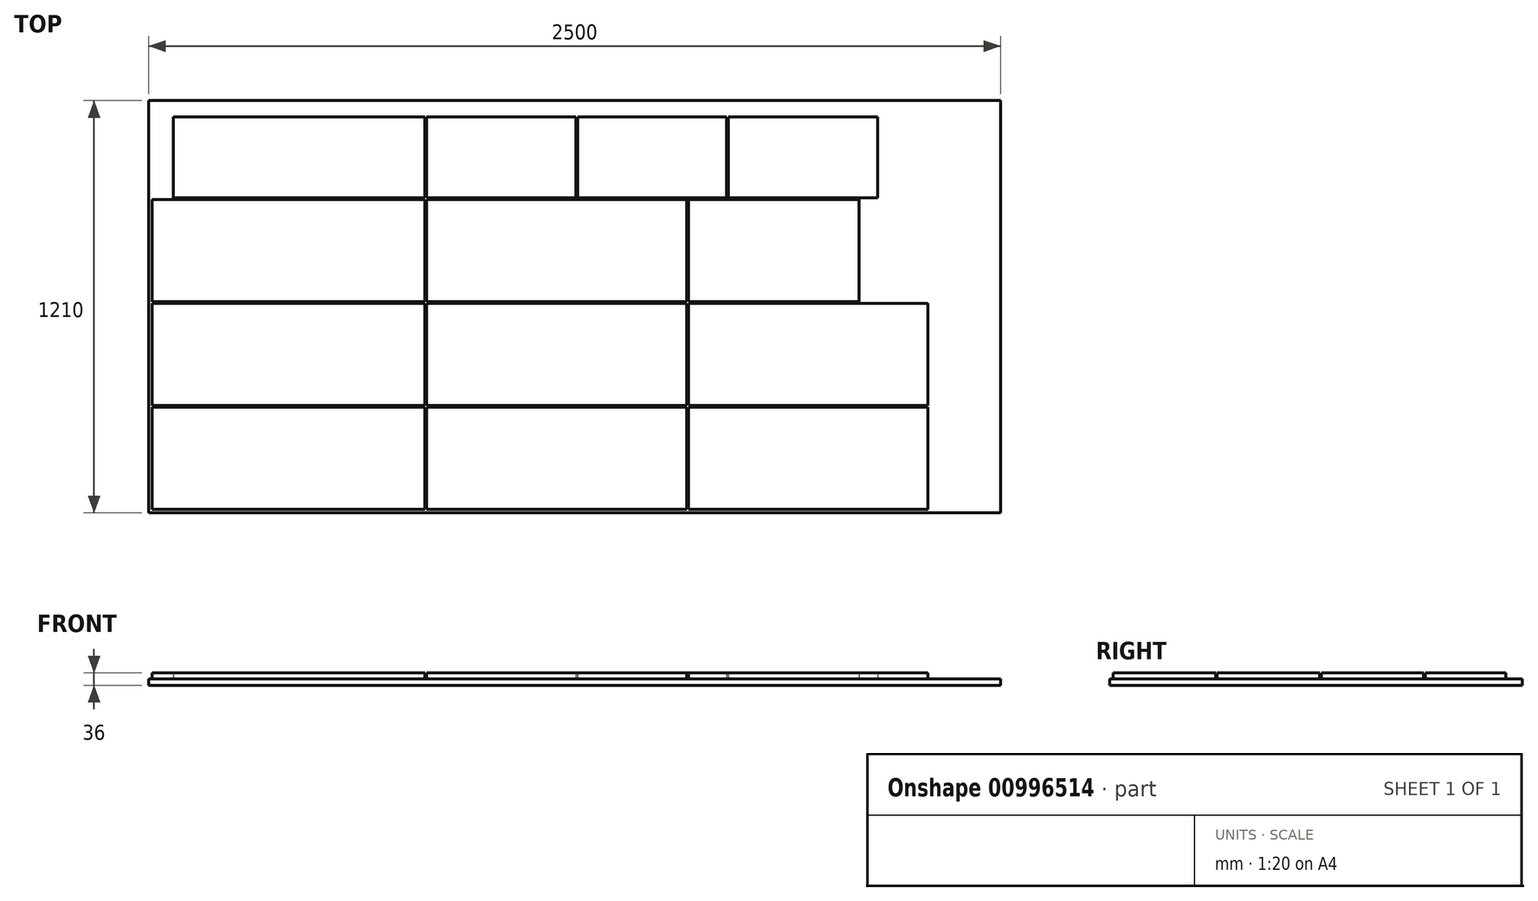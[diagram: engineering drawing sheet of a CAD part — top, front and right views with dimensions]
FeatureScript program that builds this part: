
annotation { "Feature Type Name" : "Feature", "Feature Type Description" : "" }
export const myFeature = defineFeature(function(context is Context, id is Id, definition is map)
    precondition{}
    {
        {
            var Q0;
            Q0=qCreatedBy(makeId("Top.planeOp"),FACE);
            var sketch = newSketch(context, id + "F0", { "sketchPlane" : qUnion([Q0])});
            skLineSegment(sketch, "E0.bottom", {"start": v(0, 0) * mm, "end": v(2500, 0) * mm});
            skLineSegment(sketch, "E0.top", {"start": v(0, 1210) * mm, "end": v(2500, 1210) * mm});
            skLineSegment(sketch, "E0.left", {"start": v(0, 0) * mm, "end": v(0, 1210) * mm});
            skLineSegment(sketch, "E0.right", {"start": v(2500, 0) * mm, "end": v(2500, 1210) * mm});
            skSolve(sketch);
        }
        {
            var Q0;
            Q0=makeQuery(id+"F0.imprint","IMPRINT",FACE,{"disambiguationData":[TD([[makeQuery(id+"F0.imprint","IMPRINT",EDGE,{"derivedFrom":sQuery(id+"F0.wireOp",EDGE,"E0.bottom")}),1.0]])]});
            extrude(context, id + "F1", {"entities" : qUnion([Q0]), "depth" : 18 * mm, "offsetDistance" : 25 * mm});
        }
        {
            var Q0;
            Q0=makeQuery(id+"F1.opExtrude","CAP_FACE",FACE,{"disambiguationData":[OSD([sQuery(id+"F0.wireOp",EDGE,"E0.bottom"),sQuery(id+"F0.wireOp",EDGE,"E0.top"),sQuery(id+"F0.wireOp",EDGE,"E0.left"),sQuery(id+"F0.wireOp",EDGE,"E0.right")])],"isStart":false});
            var sketch = newSketch(context, id + "F2", { "sketchPlane" : qUnion([Q0])});
            skLineSegment(sketch, "E1.bottom", {"start": v(10, 10) * mm, "end": v(810, 10) * mm});
            skLineSegment(sketch, "E1.top", {"start": v(10, 310) * mm, "end": v(810, 310) * mm});
            skLineSegment(sketch, "E1.left", {"start": v(10, 10) * mm, "end": v(10, 310) * mm});
            skLineSegment(sketch, "E1.right", {"start": v(810, 10) * mm, "end": v(810, 310) * mm});
            skLineSegment(sketch, "E2.bottom", {"start": v(10, 315) * mm, "end": v(810, 315) * mm});
            skLineSegment(sketch, "E2.top", {"start": v(10, 615) * mm, "end": v(810, 615) * mm});
            skLineSegment(sketch, "E2.left", {"start": v(10, 315) * mm, "end": v(10, 615) * mm});
            skLineSegment(sketch, "E2.right", {"start": v(810, 315) * mm, "end": v(810, 615) * mm});
            skLineSegment(sketch, "E3.bottom", {"start": v(10, 620) * mm, "end": v(810, 620) * mm});
            skLineSegment(sketch, "E3.top", {"start": v(10, 920) * mm, "end": v(810, 920) * mm});
            skLineSegment(sketch, "E3.left", {"start": v(10, 620) * mm, "end": v(10, 920) * mm});
            skLineSegment(sketch, "E3.right", {"start": v(810, 620) * mm, "end": v(810, 920) * mm});
            skLineSegment(sketch, "E4.bottom", {"start": v(815, 10) * mm, "end": v(1579, 10) * mm});
            skLineSegment(sketch, "E4.top", {"start": v(815, 310) * mm, "end": v(1579, 310) * mm});
            skLineSegment(sketch, "E4.left", {"start": v(815, 10) * mm, "end": v(815, 310) * mm});
            skLineSegment(sketch, "E4.right", {"start": v(1579, 10) * mm, "end": v(1579, 310) * mm});
            skLineSegment(sketch, "E5.bottom", {"start": v(815, 615) * mm, "end": v(1579, 615) * mm});
            skLineSegment(sketch, "E5.top", {"start": v(815, 315) * mm, "end": v(1579, 315) * mm});
            skLineSegment(sketch, "E5.left", {"start": v(815, 615) * mm, "end": v(815, 315) * mm});
            skLineSegment(sketch, "E5.right", {"start": v(1579, 615) * mm, "end": v(1579, 315) * mm});
            skLineSegment(sketch, "E6.bottom", {"start": v(815, 620) * mm, "end": v(1579, 620) * mm});
            skLineSegment(sketch, "E6.top", {"start": v(815, 920) * mm, "end": v(1579, 920) * mm});
            skLineSegment(sketch, "E6.left", {"start": v(815, 620) * mm, "end": v(815, 920) * mm});
            skLineSegment(sketch, "E6.right", {"start": v(1579, 620) * mm, "end": v(1579, 920) * mm});
            skLineSegment(sketch, "E7.bottom", {"start": v(72, 925) * mm, "end": v(810, 925) * mm});
            skLineSegment(sketch, "E7.top", {"start": v(72, 1162) * mm, "end": v(810, 1162) * mm});
            skLineSegment(sketch, "E7.left", {"start": v(72, 925) * mm, "end": v(72, 1162) * mm});
            skLineSegment(sketch, "E7.right", {"start": v(810, 925) * mm, "end": v(810, 1162) * mm});
            skLineSegment(sketch, "E8.bottom", {"start": v(815, 925) * mm, "end": v(1253, 925) * mm});
            skLineSegment(sketch, "E8.top", {"start": v(815, 1162) * mm, "end": v(1253, 1162) * mm});
            skLineSegment(sketch, "E8.left", {"start": v(815, 925) * mm, "end": v(815, 1162) * mm});
            skLineSegment(sketch, "E8.right", {"start": v(1253, 925) * mm, "end": v(1253, 1162) * mm});
            skLineSegment(sketch, "E9.bottom", {"start": v(1584, 310) * mm, "end": v(2286, 310) * mm});
            skLineSegment(sketch, "E9.top", {"start": v(1584, 10) * mm, "end": v(2286, 10) * mm});
            skLineSegment(sketch, "E9.left", {"start": v(1584, 310) * mm, "end": v(1584, 10) * mm});
            skLineSegment(sketch, "E9.right", {"start": v(2286, 310) * mm, "end": v(2286, 10) * mm});
            skLineSegment(sketch, "E10.bottom", {"start": v(1584, 615) * mm, "end": v(2286, 615) * mm});
            skLineSegment(sketch, "E10.top", {"start": v(1584, 315) * mm, "end": v(2286, 315) * mm});
            skLineSegment(sketch, "E10.left", {"start": v(1584, 615) * mm, "end": v(1584, 315) * mm});
            skLineSegment(sketch, "E10.right", {"start": v(2286, 615) * mm, "end": v(2286, 315) * mm});
            skLineSegment(sketch, "E11.bottom", {"start": v(1584, 920) * mm, "end": v(2084, 920) * mm});
            skLineSegment(sketch, "E11.top", {"start": v(1584, 620) * mm, "end": v(2084, 620) * mm});
            skLineSegment(sketch, "E11.left", {"start": v(1584, 920) * mm, "end": v(1584, 620) * mm});
            skLineSegment(sketch, "E11.right", {"start": v(2084, 920) * mm, "end": v(2084, 620) * mm});
            skLineSegment(sketch, "E12.bottom", {"start": v(1258, 1162) * mm, "end": v(1696, 1162) * mm});
            skLineSegment(sketch, "E12.top", {"start": v(1258, 925) * mm, "end": v(1696, 925) * mm});
            skLineSegment(sketch, "E12.left", {"start": v(1258, 1162) * mm, "end": v(1258, 925) * mm});
            skLineSegment(sketch, "E12.right", {"start": v(1696, 1162) * mm, "end": v(1696, 925) * mm});
            skLineSegment(sketch, "E13.bottom", {"start": v(1701, 1162) * mm, "end": v(2139, 1162) * mm});
            skLineSegment(sketch, "E13.top", {"start": v(1701, 925) * mm, "end": v(2139, 925) * mm});
            skLineSegment(sketch, "E13.left", {"start": v(1701, 1162) * mm, "end": v(1701, 925) * mm});
            skLineSegment(sketch, "E13.right", {"start": v(2139, 1162) * mm, "end": v(2139, 925) * mm});
            skSolve(sketch);
        }
        {
            var Q0;
            Q0=makeQuery(id+"F2.imprint","IMPRINT",FACE,{"disambiguationData":[TD([[makeQuery(id+"F2.imprint","IMPRINT",EDGE,{"derivedFrom":sQuery(id+"F2.wireOp",EDGE,"E7.bottom")}),1.0]])]});
            var Q1;
            Q1=makeQuery(id+"F2.imprint","IMPRINT",FACE,{"disambiguationData":[TD([[makeQuery(id+"F2.imprint","IMPRINT",EDGE,{"derivedFrom":sQuery(id+"F2.wireOp",EDGE,"E3.bottom")}),1.0]])]});
            var Q2;
            Q2=makeQuery(id+"F2.imprint","IMPRINT",FACE,{"disambiguationData":[TD([[makeQuery(id+"F2.imprint","IMPRINT",EDGE,{"derivedFrom":sQuery(id+"F2.wireOp",EDGE,"E2.bottom")}),1.0]])]});
            var Q3;
            Q3=makeQuery(id+"F2.imprint","IMPRINT",FACE,{"disambiguationData":[TD([[makeQuery(id+"F2.imprint","IMPRINT",EDGE,{"derivedFrom":sQuery(id+"F2.wireOp",EDGE,"E1.bottom")}),1.0]])]});
            var Q4;
            Q4=makeQuery(id+"F2.imprint","IMPRINT",FACE,{"disambiguationData":[TD([[makeQuery(id+"F2.imprint","IMPRINT",EDGE,{"derivedFrom":sQuery(id+"F2.wireOp",EDGE,"E4.bottom")}),1.0]])]});
            var Q5;
            Q5=makeQuery(id+"F2.imprint","IMPRINT",FACE,{"disambiguationData":[TD([[makeQuery(id+"F2.imprint","IMPRINT",EDGE,{"derivedFrom":sQuery(id+"F2.wireOp",EDGE,"E5.bottom")}),-1.0]])]});
            var Q6;
            Q6=makeQuery(id+"F2.imprint","IMPRINT",FACE,{"disambiguationData":[TD([[makeQuery(id+"F2.imprint","IMPRINT",EDGE,{"derivedFrom":sQuery(id+"F2.wireOp",EDGE,"E6.bottom")}),1.0]])]});
            var Q7;
            Q7=makeQuery(id+"F2.imprint","IMPRINT",FACE,{"disambiguationData":[TD([[makeQuery(id+"F2.imprint","IMPRINT",EDGE,{"derivedFrom":sQuery(id+"F2.wireOp",EDGE,"E8.bottom")}),1.0]])]});
            var Q8;
            Q8=makeQuery(id+"F2.imprint","IMPRINT",FACE,{"disambiguationData":[TD([[makeQuery(id+"F2.imprint","IMPRINT",EDGE,{"derivedFrom":sQuery(id+"F2.wireOp",EDGE,"E12.bottom")}),-1.0]])]});
            var Q9;
            Q9=makeQuery(id+"F2.imprint","IMPRINT",FACE,{"disambiguationData":[TD([[makeQuery(id+"F2.imprint","IMPRINT",EDGE,{"derivedFrom":sQuery(id+"F2.wireOp",EDGE,"E13.bottom")}),-1.0]])]});
            var Q10;
            Q10=makeQuery(id+"F2.imprint","IMPRINT",FACE,{"disambiguationData":[TD([[makeQuery(id+"F2.imprint","IMPRINT",EDGE,{"derivedFrom":sQuery(id+"F2.wireOp",EDGE,"E11.bottom")}),-1.0]])]});
            var Q11;
            Q11=makeQuery(id+"F2.imprint","IMPRINT",FACE,{"disambiguationData":[TD([[makeQuery(id+"F2.imprint","IMPRINT",EDGE,{"derivedFrom":sQuery(id+"F2.wireOp",EDGE,"E10.bottom")}),-1.0]])]});
            var Q12;
            Q12=makeQuery(id+"F2.imprint","IMPRINT",FACE,{"disambiguationData":[TD([[makeQuery(id+"F2.imprint","IMPRINT",EDGE,{"derivedFrom":sQuery(id+"F2.wireOp",EDGE,"E9.bottom")}),-1.0]])]});
            extrude(context, id + "F3", {"entities" : qUnion([Q0, Q1, Q2, Q3, Q4, Q5, Q6, Q7, Q8, Q9, Q10, Q11, Q12]), "depth" : 18 * mm, "offsetDistance" : 25 * mm});
        }
    });
